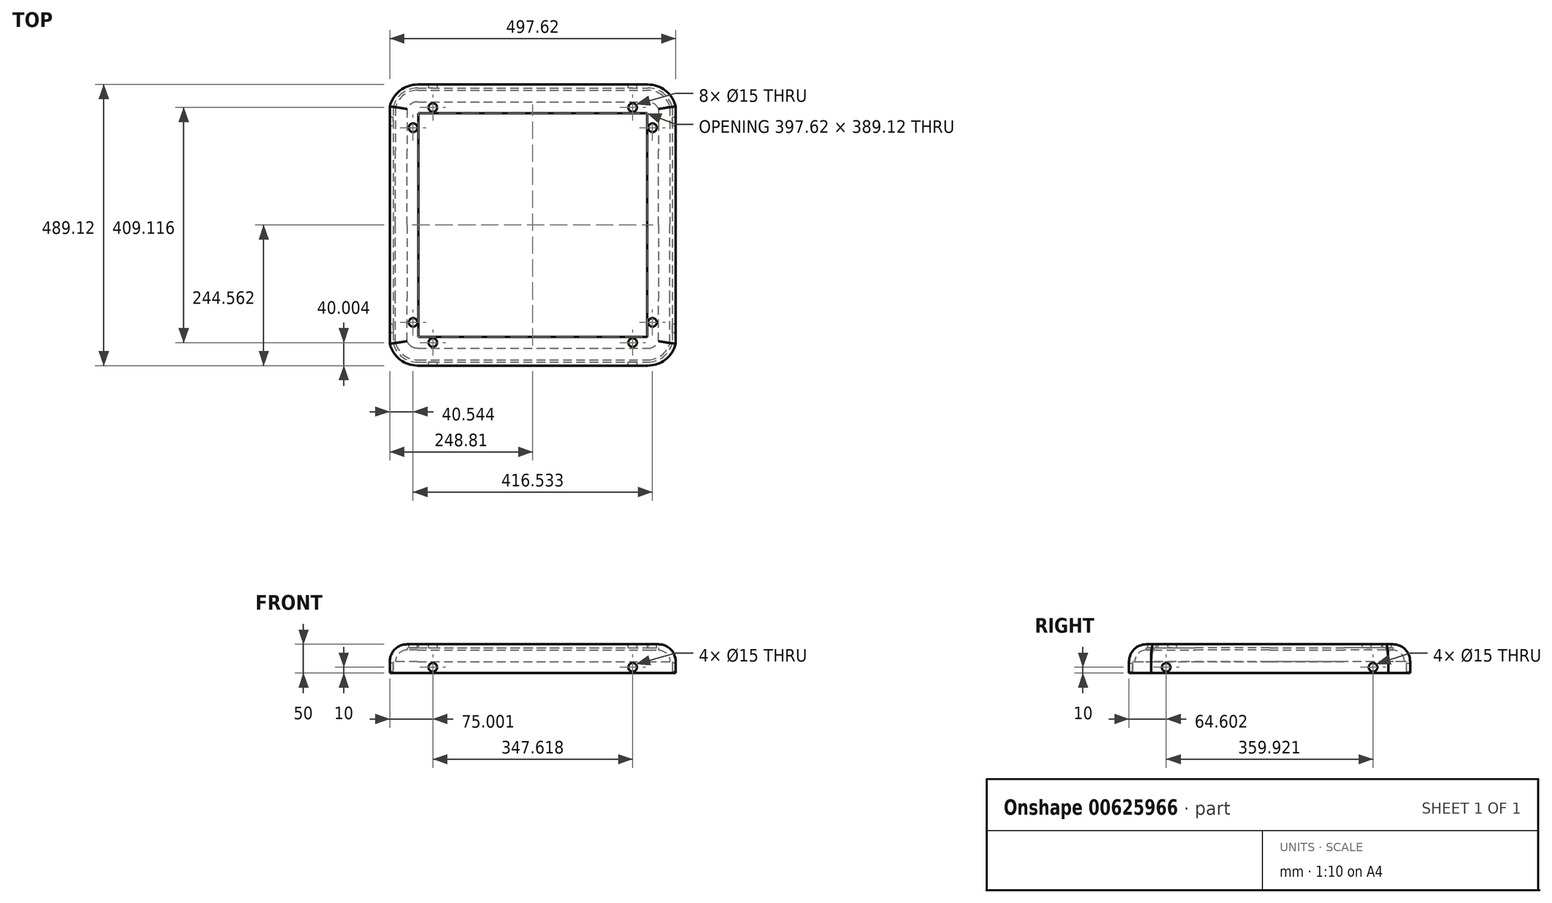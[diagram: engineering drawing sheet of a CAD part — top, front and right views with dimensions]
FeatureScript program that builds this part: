
annotation { "Feature Type Name" : "Feature", "Feature Type Description" : "" }
export const myFeature = defineFeature(function(context is Context, id is Id, definition is map)
    precondition{}
    {
        {
            var Q0;
            Q0=qCreatedBy(makeId("Right.planeOp"),FACE);
            var sketch = newSketch(context, id + "F0", { "sketchPlane" : qUnion([Q0])});
            skLineSegment(sketch, "E0.bottom", {"start": v(-6, 0) * mm, "end": v(0, 0) * mm});
            skLineSegment(sketch, "E0.left", {"start": v(0, 0) * mm, "end": v(0, 20) * mm});
            skLineSegment(sketch, "E1.top", {"start": v(-30, 50) * mm, "end": v(-50, 50) * mm});
            skLineSegment(sketch, "E1.right", {"start": v(-50, 44) * mm, "end": v(-50, 50) * mm});
            skPoint(sketch, "E2.visualSharp", {"position": v(-10, 40) * mm});
            skArc(sketch, "E3", {"start": v(-10, 20) * mm, "mid": v(-15.86, 34.14) * mm, "end": v(-30, 40) * mm});
            skArc(sketch, "E4", {"start": v(0, 20) * mm, "mid": v(-8.79, 41.21) * mm, "end": v(-30, 50) * mm});
            skLineSegment(sketch, "E5.top", {"start": v(-50, 44) * mm, "end": v(-30, 44) * mm});
            skLineSegment(sketch, "E5.right", {"start": v(-30, 40) * mm, "end": v(-30, 44) * mm});
            skLineSegment(sketch, "E6.top", {"start": v(-10, 20) * mm, "end": v(-6, 20) * mm});
            skLineSegment(sketch, "E6.right", {"start": v(-6, 0) * mm, "end": v(-6, 20) * mm});
            skSolve(sketch);
        }
        {
            var Q0;
            Q0=qCreatedBy(makeId("Top.planeOp"),FACE);
            var sketch = newSketch(context, id + "F1", { "sketchPlane" : qUnion([Q0])});
            skLineSegment(sketch, "E7", {"start": v(0, 0) * mm, "end": v(200.23, 0) * mm});
            skLineSegment(sketch, "E8", {"start": v(248.8, -115.56) * mm, "end": v(248.8, -38.18) * mm});
            skArc(sketch, "E9", {"start": v(248.8, -38.18) * mm, "mid": v(231.12, -10.69) * mm, "end": v(200.23, 0) * mm});
            skSolve(sketch);
        }
        {
            var Q0;
            Q0=makeQuery(id+"F0.imprint","IMPRINT",FACE,{"disambiguationData":[TD([[makeQuery(id+"F0.imprint","IMPRINT",EDGE,{"derivedFrom":sQuery(id+"F0.wireOp",EDGE,"E0.bottom")}),1.0]])]});
            var Q1;
            Q1=sQuery(id+"F1.wireOp",EDGE,"E7");
            var Q2;
            Q2=sQuery(id+"F1.wireOp",EDGE,"E9");
            var Q3;
            Q3=sQuery(id+"F1.wireOp",EDGE,"E8");
            sweep(context, id + "F2", {"profiles" : qUnion([Q0]), "path" : qUnion([Q1, Q2, Q3])});
        }
        {
            var Q0;
            Q0=makeQuery(id+"F2.opSweep","SWEPT_BODY",BODY,{"disambiguationData":[OSD([sQuery(id+"F0.wireOp",EDGE,"E0.bottom"),sQuery(id+"F0.wireOp",EDGE,"E0.left"),sQuery(id+"F0.wireOp",EDGE,"E0.right"),sQuery(id+"F0.wireOp",EDGE,"E1.bottom"),sQuery(id+"F0.wireOp",EDGE,"E1.top"),sQuery(id+"F0.wireOp",EDGE,"E1.right"),sQuery(id+"F0.wireOp",EDGE,"E3"),sQuery(id+"F0.wireOp",EDGE,"E4"),sQuery(id+"F1.wireOp",EDGE,"E8")])]});
            var Q1;
            Q1=qCreatedBy(makeId("Right.planeOp"),FACE);
            mirror(context, id + "F3", {"operationType" : NewBodyOperationType.ADD, "entities" : qUnion([Q0]), "mirrorPlane" : qUnion([Q1])});
        }
        {
            var Q0;
            Q0=makeQuery(id+"F3.opPattern","COPY",FACE,{"derivedFrom":makeQuery(id+"F2.opSweep","CAP_FACE",FACE,{"disambiguationData":[OSD([sQuery(id+"F0.wireOp",EDGE,"E0.bottom"),sQuery(id+"F0.wireOp",EDGE,"E0.left"),sQuery(id+"F0.wireOp",EDGE,"E0.right"),sQuery(id+"F0.wireOp",EDGE,"E1.bottom"),sQuery(id+"F0.wireOp",EDGE,"E1.top"),sQuery(id+"F0.wireOp",EDGE,"E1.right"),sQuery(id+"F0.wireOp",EDGE,"E3"),sQuery(id+"F0.wireOp",EDGE,"E4"),sQuery(id+"F1.wireOp",VERTEX,"E8.start")])],"isStart":false}),"instanceName":"1"});
            extrude(context, id + "F4", {"entities" : qUnion([Q0]), "operationType" : NewBodyOperationType.ADD, "depth" : 129 * mm, "offsetDistance" : 25 * mm});
        }
        {
            var Q0;
            Q0=makeQuery(id+"F2.opSweep","SWEPT_BODY",BODY,{"disambiguationData":[OSD([sQuery(id+"F0.wireOp",EDGE,"E0.bottom"),sQuery(id+"F0.wireOp",EDGE,"E0.left"),sQuery(id+"F0.wireOp",EDGE,"E0.right"),sQuery(id+"F0.wireOp",EDGE,"E1.bottom"),sQuery(id+"F0.wireOp",EDGE,"E1.top"),sQuery(id+"F0.wireOp",EDGE,"E1.right"),sQuery(id+"F0.wireOp",EDGE,"E3"),sQuery(id+"F0.wireOp",EDGE,"E4"),sQuery(id+"F1.wireOp",EDGE,"E8")])]});
            var Q1;
            Q1=qCreatedBy(makeId("Right.planeOp"),FACE);
            mirror(context, id + "F5", {"operationType" : NewBodyOperationType.ADD, "entities" : qUnion([Q0]), "mirrorPlane" : qUnion([Q1])});
        }
        {
            var Q0;
            Q0=makeQuery(id+"F4.opExtrude","CAP_FACE",FACE,{"disambiguationData":[OSD([sQuery(id+"F0.wireOp",EDGE,"E0.bottom"),sQuery(id+"F0.wireOp",EDGE,"E0.left"),sQuery(id+"F0.wireOp",EDGE,"E0.right"),sQuery(id+"F0.wireOp",EDGE,"E1.bottom"),sQuery(id+"F0.wireOp",EDGE,"E1.top"),sQuery(id+"F0.wireOp",EDGE,"E1.right"),sQuery(id+"F0.wireOp",EDGE,"E3"),sQuery(id+"F0.wireOp",EDGE,"E4"),sQuery(id+"F1.wireOp",VERTEX,"E8.start")])],"isStart":false});
            cPlane(context, id + "F6", {"entities" : qUnion([Q0]), "cplaneType" : CPlaneType.OFFSET, "offset" : 0 * mm, "oppositeDirection" : true, "width" : 150 * mm, "height" : 150 * mm});
        }
        {
            var Q0;
            Q0=makeQuery(id+"F2.opSweep","SWEPT_BODY",BODY,{"disambiguationData":[OSD([sQuery(id+"F0.wireOp",EDGE,"E0.bottom"),sQuery(id+"F0.wireOp",EDGE,"E0.left"),sQuery(id+"F0.wireOp",EDGE,"E0.right"),sQuery(id+"F0.wireOp",EDGE,"E1.bottom"),sQuery(id+"F0.wireOp",EDGE,"E1.top"),sQuery(id+"F0.wireOp",EDGE,"E1.right"),sQuery(id+"F0.wireOp",EDGE,"E3"),sQuery(id+"F0.wireOp",EDGE,"E4"),sQuery(id+"F1.wireOp",EDGE,"E8")])]});
            var Q1;
            Q1=qCreatedBy(id+"F6.planeOp",FACE);
            mirror(context, id + "F7", {"operationType" : NewBodyOperationType.ADD, "entities" : qUnion([Q0]), "mirrorPlane" : qUnion([Q1])});
        }
        {
            var Q0;
            {var subQ0=sQuery(id+"F0.wireOp",EDGE,"E1.top");var subQ1=makeQuery(id+"F2.opSweep","SWEPT_FACE",FACE,{"disambiguationData":[OSD([subQ0,sQuery(id+"F1.wireOp",EDGE,"E7")])]});var subQ2=makeQuery(id+"F4.boolean.opBoolean","MERGE",FACE,{"derivedFrom":[makeQuery(id+"F3.boolean.opBoolean","MERGE",FACE,{"derivedFrom":[subQ1,makeQuery(id+"F3.opPattern","COPY",FACE,{"derivedFrom":subQ1,"instanceName":"1"})]}),makeQuery(id+"F4.opExtrude","SWEPT_FACE",FACE,{"disambiguationData":[OSD([subQ0,sQuery(id+"F1.wireOp",VERTEX,"E8.start")])]})]});var subQ3=makeQuery(id+"F5.boolean.opBoolean","MERGE",FACE,{"derivedFrom":[subQ2,makeQuery(id+"F5.opPattern","COPY",FACE,{"derivedFrom":subQ2,"instanceName":"1"})]});Q0=makeQuery(id+"F7.boolean.opBoolean","MERGE",FACE,{"derivedFrom":[subQ3,makeQuery(id+"F7.opPattern","COPY",FACE,{"derivedFrom":subQ3,"instanceName":"1"})]});}
            var sketch = newSketch(context, id + "F8", { "sketchPlane" : qUnion([Q0])});
            skCircle(sketch, "E10", {"center": v(-173.8, -40) * mm, "radius": 7.4 * mm});
            skLineSegment(sketch, "E11", {"start": v(-191.13, -30) * mm, "end": v(-160.39, -30) * mm, "construction": true});
            skLineSegment(sketch, "E12", {"start": v(-188.28, -50) * mm, "end": v(-161.95, -50) * mm, "construction": true});
            skLineSegment(sketch, "E13", {"start": v(-218.8, -42.6) * mm, "end": v(-218.8, -59.38) * mm, "construction": true});
            skLineSegment(sketch, "E14", {"start": v(-198.8, -50) * mm, "end": v(198.8, -439.12) * mm, "construction": true});
            skCircle(sketch, "E15.MirrorC", {"center": v(-208.27, -75.21) * mm, "radius": 7.4 * mm});
            skLineSegment(sketch, "E16", {"start": v(198.8, -50) * mm, "end": v(-198.8, -439.12) * mm, "construction": true});
            skLineSegment(sketch, "E17", {"start": v(0, -244.56) * mm, "end": v(0, -50) * mm, "construction": true});
            skCircle(sketch, "E18.MirrorC", {"center": v(173.8, -40) * mm, "radius": 7.4 * mm});
            skCircle(sketch, "E19.MirrorC", {"center": v(208.27, -75.21) * mm, "radius": 7.4 * mm});
            skLineSegment(sketch, "E20", {"start": v(0, -244.56) * mm, "end": v(-198.8, -244.56) * mm, "construction": true});
            skCircle(sketch, "E21.MirrorC", {"center": v(-173.8, -449.12) * mm, "radius": 7.4 * mm});
            skCircle(sketch, "E22.MirrorC", {"center": v(-208.27, -413.9) * mm, "radius": 7.4 * mm});
            skCircle(sketch, "E23.MirrorC", {"center": v(208.27, -413.9) * mm, "radius": 7.4 * mm});
            skCircle(sketch, "E24.MirrorC", {"center": v(173.8, -449.12) * mm, "radius": 7.4 * mm});
            skSolve(sketch);
        }
        {
            var Q0;
            Q0=sQuery(id+"F8.wireOp",VERTEX,"E15.MirrorC.center");
            var Q1;
            Q1=sQuery(id+"F8.wireOp",VERTEX,"E10.center");
            var Q2;
            Q2=sQuery(id+"F8.wireOp",VERTEX,"E18.MirrorC.center");
            var Q3;
            Q3=sQuery(id+"F8.wireOp",VERTEX,"E19.MirrorC.center");
            var Q4;
            Q4=sQuery(id+"F8.wireOp",VERTEX,"E22.MirrorC.center");
            var Q5;
            Q5=sQuery(id+"F8.wireOp",VERTEX,"E21.MirrorC.center");
            var Q6;
            Q6=sQuery(id+"F8.wireOp",VERTEX,"E24.MirrorC.center");
            var Q7;
            Q7=sQuery(id+"F8.wireOp",VERTEX,"E23.MirrorC.center");
            var Q8;
            Q8=makeQuery(id+"F2.opSweep","SWEPT_BODY",BODY,{"disambiguationData":[OSD([sQuery(id+"F0.wireOp",EDGE,"E0.bottom"),sQuery(id+"F0.wireOp",EDGE,"E0.left"),sQuery(id+"F0.wireOp",EDGE,"E1.top"),sQuery(id+"F0.wireOp",EDGE,"E1.right"),sQuery(id+"F0.wireOp",EDGE,"E3"),sQuery(id+"F0.wireOp",EDGE,"E4"),sQuery(id+"F0.wireOp",EDGE,"E5.top"),sQuery(id+"F0.wireOp",EDGE,"E5.right"),sQuery(id+"F0.wireOp",EDGE,"E6.top"),sQuery(id+"F0.wireOp",EDGE,"E6.right"),sQuery(id+"F1.wireOp",EDGE,"E8")])]});
            hole(context, id + "F9", {"style" : HoleStyle.SIMPLE, "endStyle" : HoleEndStyle.THROUGH, "holeDiameter" : 15 * mm, "majorDiameter" : 5 * mm, "isTappedThrough" : true, "tappedDepth" : 12 * mm, "tapClearance" : 3, "locations" : qUnion([Q0, Q1, Q2, Q3, Q4, Q5, Q6, Q7]), "scope" : qUnion([Q8])});
        }
        {
            var Q0;
            {var subQ0=makeQuery(id+"F2.opSweep","SWEPT_FACE",FACE,{"disambiguationData":[OSD([sQuery(id+"F0.wireOp",EDGE,"E0.left"),sQuery(id+"F1.wireOp",EDGE,"E7")])]});Q0=makeQuery(id+"F3.boolean.opBoolean","MERGE",FACE,{"derivedFrom":[subQ0,makeQuery(id+"F3.opPattern","COPY",FACE,{"derivedFrom":subQ0,"instanceName":"1"})]});}
            var sketch = newSketch(context, id + "F10", { "sketchPlane" : qUnion([Q0])});
            skLineSegment(sketch, "E25", {"start": v(-200.23, 20) * mm, "end": v(-145.16, 20) * mm, "construction": true});
            skLineSegment(sketch, "E26", {"start": v(-200.23, 0) * mm, "end": v(-141.48, 0) * mm, "construction": true});
            skCircle(sketch, "E27", {"center": v(-173.8, 10) * mm, "radius": 6.72 * mm});
            skCircle(sketch, "E28.MirrorC", {"center": v(173.8, 10) * mm, "radius": 6.72 * mm});
            skSolve(sketch);
        }
        {
            var Q0;
            Q0=sQuery(id+"F10.wireOp",VERTEX,"E27.center");
            var Q1;
            Q1=sQuery(id+"F10.wireOp",VERTEX,"E28.MirrorC.center");
            var Q2;
            Q2=makeQuery(id+"F2.opSweep","SWEPT_BODY",BODY,{"disambiguationData":[OSD([sQuery(id+"F0.wireOp",EDGE,"E0.bottom"),sQuery(id+"F0.wireOp",EDGE,"E0.left"),sQuery(id+"F0.wireOp",EDGE,"E1.top"),sQuery(id+"F0.wireOp",EDGE,"E1.right"),sQuery(id+"F0.wireOp",EDGE,"E3"),sQuery(id+"F0.wireOp",EDGE,"E4"),sQuery(id+"F0.wireOp",EDGE,"E5.top"),sQuery(id+"F0.wireOp",EDGE,"E5.right"),sQuery(id+"F0.wireOp",EDGE,"E6.top"),sQuery(id+"F0.wireOp",EDGE,"E6.right"),sQuery(id+"F1.wireOp",EDGE,"E8")])]});
            hole(context, id + "F11", {"style" : HoleStyle.SIMPLE, "endStyle" : HoleEndStyle.THROUGH, "holeDiameter" : 15 * mm, "majorDiameter" : 5 * mm, "isTappedThrough" : true, "tappedDepth" : 12 * mm, "tapClearance" : 3, "locations" : qUnion([Q0, Q1]), "scope" : qUnion([Q2])});
        }
        {
            var Q0;
            {var subQ0=sQuery(id+"F0.wireOp",EDGE,"E0.left");var subQ1=makeQuery(id+"F4.boolean.opBoolean","MERGE",FACE,{"derivedFrom":[makeQuery(id+"F3.opPattern","COPY",FACE,{"derivedFrom":makeQuery(id+"F2.opSweep","SWEPT_FACE",FACE,{"disambiguationData":[OSD([subQ0,sQuery(id+"F1.wireOp",EDGE,"E8")])]}),"instanceName":"1"}),makeQuery(id+"F4.opExtrude","SWEPT_FACE",FACE,{"disambiguationData":[OSD([subQ0,sQuery(id+"F1.wireOp",VERTEX,"E8.start")])]})]});Q0=makeQuery(id+"F7.boolean.opBoolean","MERGE",FACE,{"derivedFrom":[subQ1,makeQuery(id+"F7.opPattern","COPY",FACE,{"derivedFrom":subQ1,"instanceName":"1"})]});}
            var sketch = newSketch(context, id + "F12", { "sketchPlane" : qUnion([Q0])});
            skLineSegment(sketch, "E29", {"start": v(38.18, 20) * mm, "end": v(85.84, 20) * mm, "construction": true});
            skLineSegment(sketch, "E30", {"start": v(38.18, 0) * mm, "end": v(87.85, 0) * mm, "construction": true});
            skCircle(sketch, "E31", {"center": v(64.6, 10) * mm, "radius": 7.64 * mm});
            skCircle(sketch, "E32.MirrorC", {"center": v(424.52, 10) * mm, "radius": 7.64 * mm});
            skSolve(sketch);
        }
        {
            var Q0;
            Q0=sQuery(id+"F12.wireOp",VERTEX,"E31.center");
            var Q1;
            Q1=sQuery(id+"F12.wireOp",VERTEX,"E32.MirrorC.center");
            var Q2;
            Q2=makeQuery(id+"F2.opSweep","SWEPT_BODY",BODY,{"disambiguationData":[OSD([sQuery(id+"F0.wireOp",EDGE,"E0.bottom"),sQuery(id+"F0.wireOp",EDGE,"E0.left"),sQuery(id+"F0.wireOp",EDGE,"E1.top"),sQuery(id+"F0.wireOp",EDGE,"E1.right"),sQuery(id+"F0.wireOp",EDGE,"E3"),sQuery(id+"F0.wireOp",EDGE,"E4"),sQuery(id+"F0.wireOp",EDGE,"E5.top"),sQuery(id+"F0.wireOp",EDGE,"E5.right"),sQuery(id+"F0.wireOp",EDGE,"E6.top"),sQuery(id+"F0.wireOp",EDGE,"E6.right"),sQuery(id+"F1.wireOp",EDGE,"E8")])]});
            hole(context, id + "F13", {"style" : HoleStyle.SIMPLE, "endStyle" : HoleEndStyle.THROUGH, "holeDiameter" : 15 * mm, "majorDiameter" : 5 * mm, "isTappedThrough" : true, "tappedDepth" : 12 * mm, "tapClearance" : 3, "locations" : qUnion([Q0, Q1]), "scope" : qUnion([Q2])});
        }
    });
